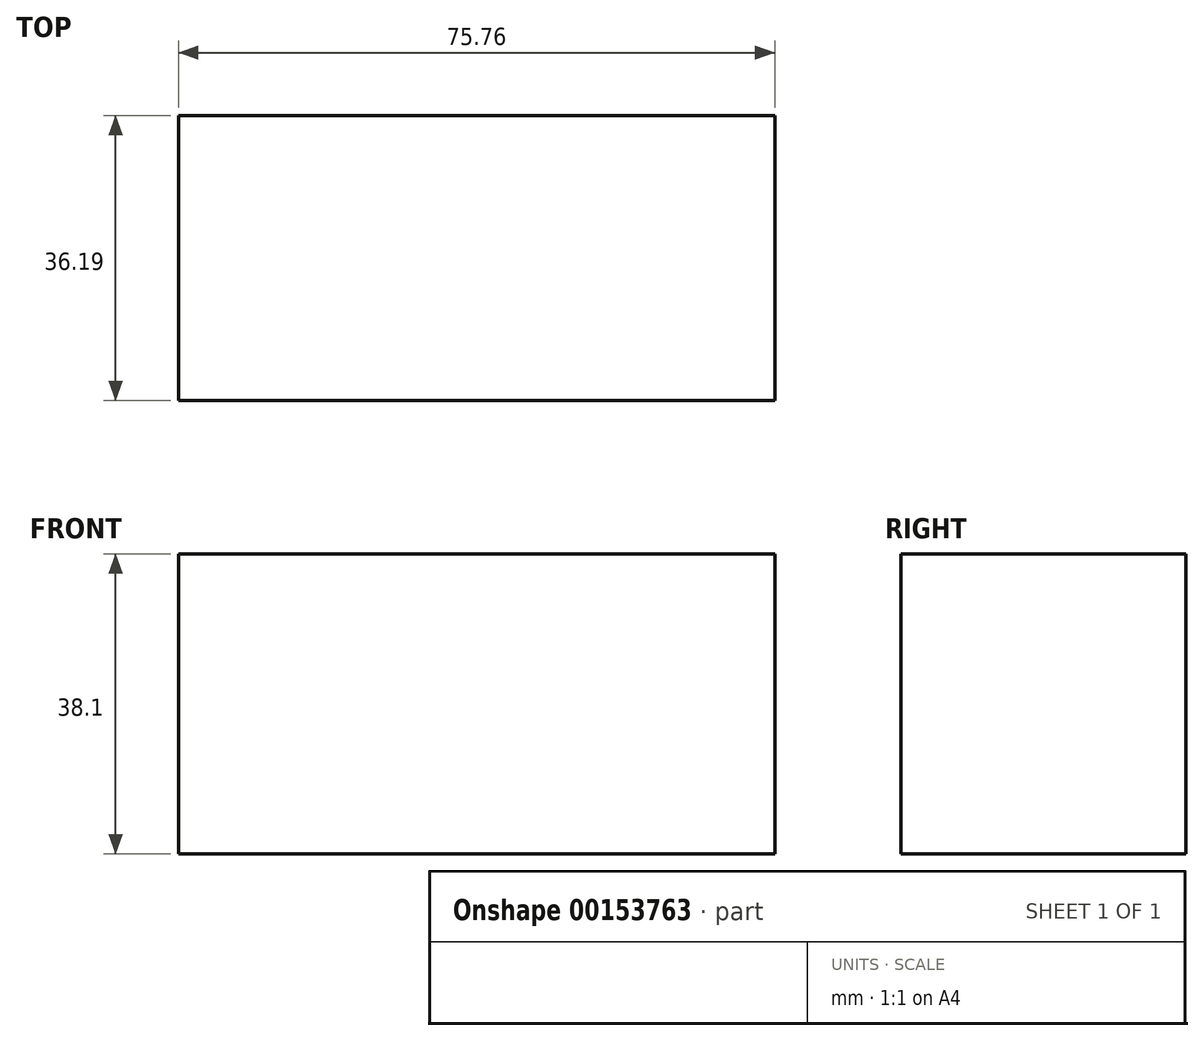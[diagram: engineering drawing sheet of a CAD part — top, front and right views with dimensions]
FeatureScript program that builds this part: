
annotation { "Feature Type Name" : "Feature", "Feature Type Description" : "" }
export const myFeature = defineFeature(function(context is Context, id is Id, definition is map)
    precondition{}
    {
        {
            var Q0;
            Q0=qCreatedBy(makeId("Top.planeOp"),FACE);
            var sketch = newSketch(context, id + "F0", { "sketchPlane" : qUnion([Q0])});
            skLineSegment(sketch, "E0.bottom", {"start": v(-29.54, 16.4) * mm, "end": v(46.22, 16.4) * mm});
            skLineSegment(sketch, "E0.top", {"start": v(-29.54, -19.8) * mm, "end": v(46.22, -19.8) * mm});
            skLineSegment(sketch, "E0.left", {"start": v(-29.54, 16.4) * mm, "end": v(-29.54, -19.8) * mm});
            skLineSegment(sketch, "E0.right", {"start": v(46.22, 16.4) * mm, "end": v(46.22, -19.8) * mm});
            skSolve(sketch);
        }
        {
            var Q0;
            Q0 = qSketchRegion(id + "F0", true);
            extrude(context, id + "F1", {"entities" : qUnion([Q0]), "depth" : 38.1 * mm});
        }
    });
